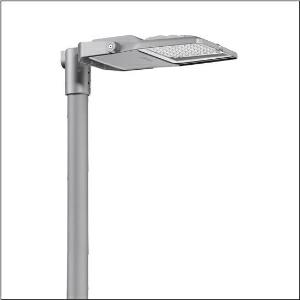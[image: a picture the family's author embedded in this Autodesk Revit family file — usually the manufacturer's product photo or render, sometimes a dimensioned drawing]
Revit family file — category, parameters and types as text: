
# Revit family: floodlight_fl_21_iq_mini___pl52_5xa7772d2d3a_9966
name_source: partatom
category: Lighting Fixtures
units: mm (PartAtom-declared; Revit-internal decimal feet)

## family parameters
Cut with Voids When Loaded = No
Host = Face
Light Source = No
Part Type = Normal
Room Calculation Point = No
Round Connector Dimension = Use Diameter
Shared = No

## types (1)
- --- (1 x LED, 17830 lm, 143 W, 3000K)
    Apparent Load = 143 VA
    CIE Flux Codes = 26 60 98 100 100
    Color Rendering = 70
    Color Temperature = 3000K
    Default Elevation = 1800 mm
    Description = Floodlight FL 21 iQ mini, floodlight, primary light control with lens, of PMMA, primary optical cover: protective disc, of toughened safety glass, transparent, light distribution: PL52, light emission: direct distribution, installation type: surface-mounted, LED, High Power LED, rated luminous flux: 17.830lm, luminous efficacy: 125lm/W, light colour: 730, colour temperature: 3000K, control: Auto-Match, Temp-Guard, Night-Set, Smart-Wire, Desk-Remote (wireless, voltage-free reading and setting of iQ features in the workshop via application-optimized NFC function/RFID function), optimised constant luminous flux control (CLO 2.0), Light-Fading, Lumen-Switch, with terminal, 6-pole, mains connection: 220..240V, AC, 50/60Hz, start of lifetime: 143W, end of service life: 152W, reduction: 61W, luminaire housing, of diecast aluminium, powder-coated, Siteco® metallic grey (DB 702S), corrosivity category C5 mid according to DIN EN ISO 12944, sealing non-destructively replaceable, please order mast flange separately, mast bracket, of steel, galvanised, powder-coated, protection rating (complete): IP66, insulation class (complete): insulation class II (safety insulation), certification: CE, ENEC, VDE, protection symbol: D, impact resistance: IK08, permissible operating ambient temperature: -40..+40°C, permissible operating ambient temperature for outdoor applications: -40..+50°C, standard: DIN EN 12944, LABS conformity tested according to VDMA 24364:2018-05, packaging unit: 1 piece

Light Distribution: PL52
    Height = 70 mm
    Lamp = 1 x LED
    Lamp Light Flux = 17830 lm
    Lamp Power = 143 W
    Lamp count = 1
    Length = 485 mm
    Luminous efficacy = 125 lm/W
    Manufacturer = Siteco
    ModVariant = No
    Model = 5XA7772D2D3A
    Number of Poles = 1
    OnlyDefault = Yes
    Power Factor = 1
    Product Name = Floodlight FL 21 iQ mini | PL52
    Product group = floodlight | pylon annexe
    ProductGroupID = 6200
    Protection Class = Protection class II
    Protection Degree = IP 66
    RLX_Detail_Level = 1
    RLX_Emergency_Light_Flux = 0 lm
    RLX_Emergency_Type = 0
    RLX_Emergency_Type_DB = No
    RlxData = <blob elided: 101785 chars, md5=c093f938>
    Socket = socket
    Standby Power = 0 W
    System Light Flux = 17830 lm
    System Power = 143 W
    Type Comments = factory setting: luminous flux: 100 % | dim-lin: 254 | 730 mA
    Type Image = l_1007125.jpg
    URL = http://relux.com
    VarID = @adj_113863
    Voltage = 0 V
    Weight = 0.00 kg
    Width = 337 mm

## geometry (parser evidence)
native form markers: Blend x4, Sweep x12
no freeform markers — native parametric forms only
